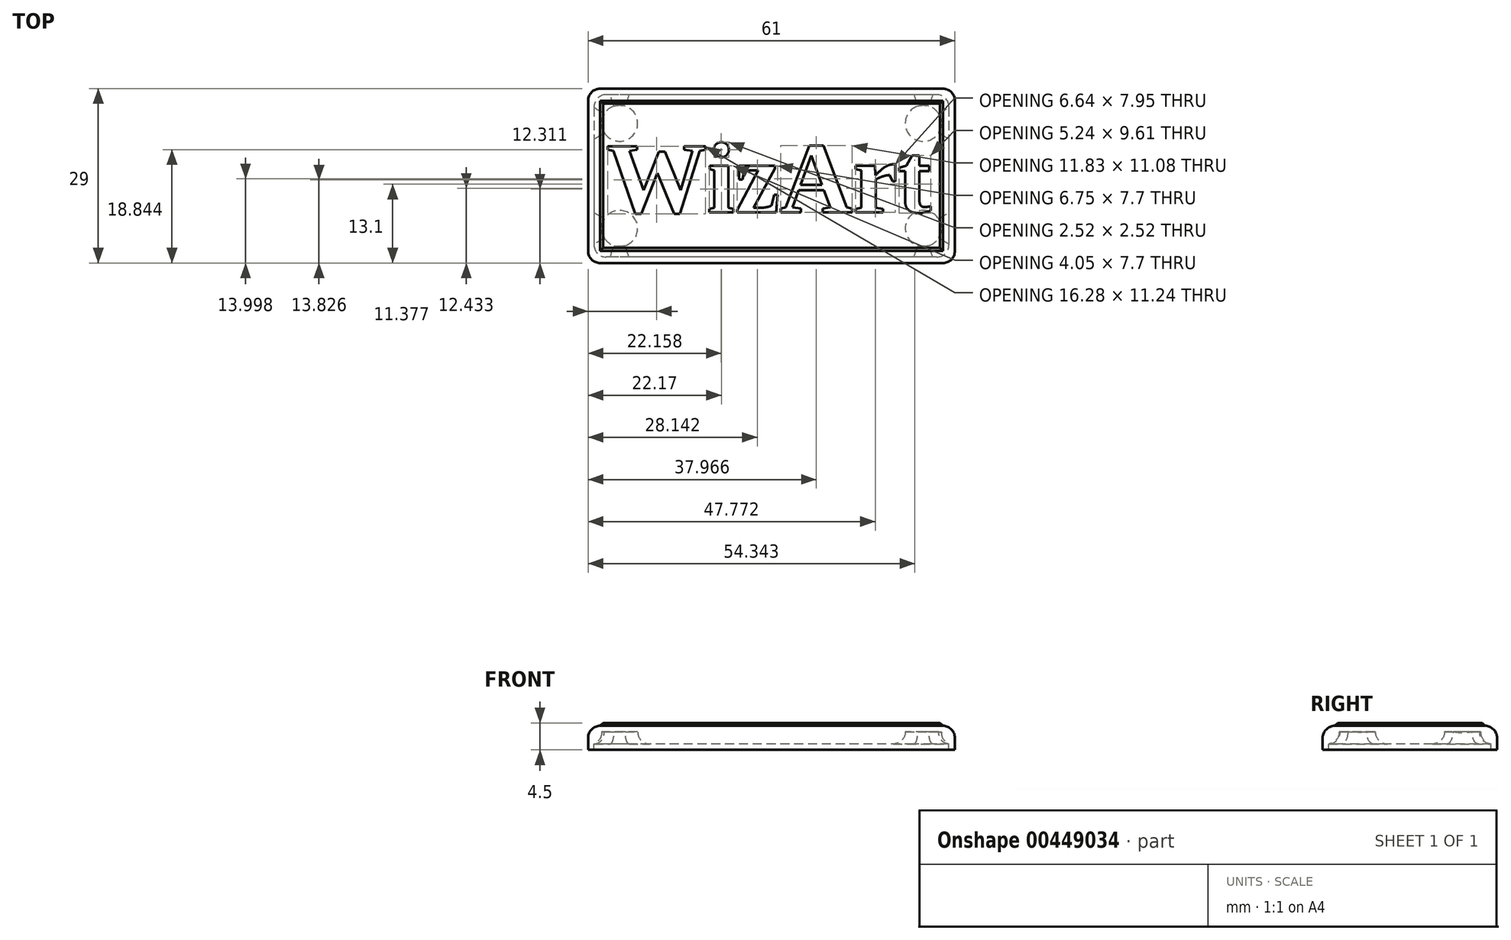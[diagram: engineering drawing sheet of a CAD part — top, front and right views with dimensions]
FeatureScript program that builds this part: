
annotation { "Feature Type Name" : "Feature", "Feature Type Description" : "" }
export const myFeature = defineFeature(function(context is Context, id is Id, definition is map)
    precondition{}
    {
        {
            var Q0;
            Q0=qCreatedBy(makeId("Top.planeOp"),FACE);
            var sketch = newSketch(context, id + "F0", { "sketchPlane" : qUnion([Q0])});
            skLineSegment(sketch, "E0.bottom", {"start": v(30.5, 14.5) * mm, "end": v(-30.5, 14.5) * mm});
            skLineSegment(sketch, "E0.top", {"start": v(30.5, -14.5) * mm, "end": v(-30.5, -14.5) * mm});
            skLineSegment(sketch, "E0.left", {"start": v(30.5, 14.5) * mm, "end": v(30.5, -14.5) * mm});
            skLineSegment(sketch, "E0.right", {"start": v(-30.5, 14.5) * mm, "end": v(-30.5, -14.5) * mm});
            skPoint(sketch, "E0.middle", {"position": v(0, 0) * mm});
            skLineSegment(sketch, "E1.bottom", {"start": v(29.5, 13.5) * mm, "end": v(-29.5, 13.5) * mm});
            skLineSegment(sketch, "E1.top", {"start": v(29.5, -13.5) * mm, "end": v(-29.5, -13.5) * mm});
            skLineSegment(sketch, "E1.left", {"start": v(29.5, 13.5) * mm, "end": v(29.5, -13.5) * mm});
            skLineSegment(sketch, "E1.right", {"start": v(-29.5, 13.5) * mm, "end": v(-29.5, -13.5) * mm});
            skLineSegment(sketch, "E2.bottom", {"start": v(25.25, 8.75) * mm, "end": v(-25.25, 8.75) * mm, "construction": true});
            skLineSegment(sketch, "E2.top", {"start": v(25.25, -8.75) * mm, "end": v(-25.25, -8.75) * mm, "construction": true});
            skLineSegment(sketch, "E2.left", {"start": v(25.25, 8.75) * mm, "end": v(25.25, -8.75) * mm, "construction": true});
            skLineSegment(sketch, "E2.right", {"start": v(-25.25, 8.75) * mm, "end": v(-25.25, -8.75) * mm, "construction": true});
            skCircle(sketch, "E3", {"center": v(-25.25, 8.75) * mm, "radius": 3 * mm});
            skCircle(sketch, "E4.MirrorC", {"center": v(25.25, 8.75) * mm, "radius": 3 * mm});
            skCircle(sketch, "E5.MirrorC", {"center": v(-25.25, -8.75) * mm, "radius": 3 * mm});
            skCircle(sketch, "E6.MirrorC", {"center": v(25.25, -8.75) * mm, "radius": 3 * mm});
            skPoint(sketch, "E7", {"position": v(-22.25, 8.75) * mm});
            skPoint(sketch, "E8", {"position": v(-22.25, -8.75) * mm});
            skPoint(sketch, "E9", {"position": v(22.25, -8.75) * mm});
            skPoint(sketch, "E10", {"position": v(22.25, 8.75) * mm});
            skSolve(sketch);
        }
        {
            var Q0;
            Q0=makeQuery(id+"F0.imprint","IMPRINT",FACE,{"disambiguationData":[TD([[makeQuery(id+"F0.imprint","IMPRINT",EDGE,{"derivedFrom":sQuery(id+"F0.wireOp",EDGE,"E1.bottom")}),1.0]])]});
            var Q1;
            Q1=makeQuery(id+"F0.imprint","IMPRINT",FACE,{"disambiguationData":[TD([[makeQuery(id+"F0.imprint","IMPRINT",EDGE,{"derivedFrom":sQuery(id+"F0.wireOp",EDGE,"E0.bottom")}),1.0]])]});
            extrude(context, id + "F1", {"entities" : qUnion([Q0, Q1]), "depth" : 2 * mm});
        }
        {
            var Q0;
            Q0=makeQuery(id+"F0.imprint","IMPRINT",FACE,{"disambiguationData":[TD([[makeQuery(id+"F0.imprint","IMPRINT",EDGE,{"derivedFrom":sQuery(id+"F0.wireOp",EDGE,"E0.bottom")}),1.0]])]});
            extrude(context, id + "F2", {"entities" : qUnion([Q0]), "operationType" : NewBodyOperationType.ADD, "oppositeDirection" : true, "depth" : 1 * mm});
        }
        {
            var Q0;
            Q0=makeQuery(id+"F1.opExtrude","CAP_FACE",FACE,{"disambiguationData":[OSD([sQuery(id+"F0.wireOp",EDGE,"E0.bottom"),sQuery(id+"F0.wireOp",EDGE,"E0.top"),sQuery(id+"F0.wireOp",EDGE,"E0.left"),sQuery(id+"F0.wireOp",EDGE,"E0.right"),sQuery(id+"F0.wireOp",EDGE,"E3"),sQuery(id+"F0.wireOp",EDGE,"E4.MirrorC"),sQuery(id+"F0.wireOp",EDGE,"E5.MirrorC"),sQuery(id+"F0.wireOp",EDGE,"E6.MirrorC")])],"isStart":false});
            var sketch = newSketch(context, id + "F3", { "sketchPlane" : qUnion([Q0])});
            skLineSegment(sketch, "E11.bottom", {"start": v(30.5, 14.5) * mm, "end": v(-30.5, 14.5) * mm});
            skLineSegment(sketch, "E11.top", {"start": v(30.5, -14.5) * mm, "end": v(-30.5, -14.5) * mm});
            skLineSegment(sketch, "E11.left", {"start": v(30.5, 14.5) * mm, "end": v(30.5, -14.5) * mm});
            skLineSegment(sketch, "E11.right", {"start": v(-30.5, 14.5) * mm, "end": v(-30.5, -14.5) * mm});
            skPoint(sketch, "E11.middle", {"position": v(0, 0) * mm});
            skSolve(sketch);
        }
        {
            var Q0;
            Q0 = qSketchRegion(id + "F3", true);
            extrude(context, id + "F4", {"entities" : qUnion([Q0]), "operationType" : NewBodyOperationType.ADD, "depth" : 1 * mm});
        }
        {
            var Q0;
            Q0=makeQuery(id+"F2.opExtrude","SWEPT_EDGE",EDGE,{"disambiguationData":[OSD([sQuery(id+"F0.wireOp",EDGE,"E1.top"),sQuery(id+"F0.wireOp",EDGE,"E1.right")])]});
            var Q1;
            Q1=makeQuery(id+"F2.opExtrude","SWEPT_EDGE",EDGE,{"disambiguationData":[OSD([sQuery(id+"F0.wireOp",EDGE,"E1.bottom"),sQuery(id+"F0.wireOp",EDGE,"E1.right")])]});
            var Q2;
            Q2=makeQuery(id+"F2.opExtrude","SWEPT_EDGE",EDGE,{"disambiguationData":[OSD([sQuery(id+"F0.wireOp",EDGE,"E1.top"),sQuery(id+"F0.wireOp",EDGE,"E1.left")])]});
            var Q3;
            Q3=makeQuery(id+"F2.opExtrude","SWEPT_EDGE",EDGE,{"disambiguationData":[OSD([sQuery(id+"F0.wireOp",EDGE,"E1.bottom"),sQuery(id+"F0.wireOp",EDGE,"E1.left")])]});
            var Q4;
            {var subQ0=sQuery(id+"F0.wireOp",EDGE,"E0.right");var subQ1=sQuery(id+"F0.wireOp",EDGE,"E0.top");Q4=makeQuery(id+"F4.boolean.opBoolean","MERGE",EDGE,{"derivedFrom":[makeQuery(id+"F2.boolean.opBoolean","MERGE",EDGE,{"derivedFrom":[makeQuery(id+"F1.opExtrude","SWEPT_EDGE",EDGE,{"disambiguationData":[OSD([subQ1,subQ0])]}),makeQuery(id+"F2.opExtrude","SWEPT_EDGE",EDGE,{"disambiguationData":[OSD([subQ1,subQ0])]})]}),makeQuery(id+"F4.opExtrude","SWEPT_EDGE",EDGE,{"disambiguationData":[OSD([sQuery(id+"F3.wireOp",EDGE,"E11.top"),sQuery(id+"F3.wireOp",EDGE,"E11.right")])]})]});}
            var Q5;
            {var subQ0=sQuery(id+"F0.wireOp",EDGE,"E0.right");var subQ1=sQuery(id+"F0.wireOp",EDGE,"E0.bottom");Q5=makeQuery(id+"F4.boolean.opBoolean","MERGE",EDGE,{"derivedFrom":[makeQuery(id+"F2.boolean.opBoolean","MERGE",EDGE,{"derivedFrom":[makeQuery(id+"F1.opExtrude","SWEPT_EDGE",EDGE,{"disambiguationData":[OSD([subQ1,subQ0])]}),makeQuery(id+"F2.opExtrude","SWEPT_EDGE",EDGE,{"disambiguationData":[OSD([subQ1,subQ0])]})]}),makeQuery(id+"F4.opExtrude","SWEPT_EDGE",EDGE,{"disambiguationData":[OSD([sQuery(id+"F3.wireOp",EDGE,"E11.bottom"),sQuery(id+"F3.wireOp",EDGE,"E11.right")])]})]});}
            var Q6;
            {var subQ0=sQuery(id+"F0.wireOp",EDGE,"E0.left");var subQ1=sQuery(id+"F0.wireOp",EDGE,"E0.bottom");Q6=makeQuery(id+"F4.boolean.opBoolean","MERGE",EDGE,{"derivedFrom":[makeQuery(id+"F2.boolean.opBoolean","MERGE",EDGE,{"derivedFrom":[makeQuery(id+"F1.opExtrude","SWEPT_EDGE",EDGE,{"disambiguationData":[OSD([subQ1,subQ0])]}),makeQuery(id+"F2.opExtrude","SWEPT_EDGE",EDGE,{"disambiguationData":[OSD([subQ1,subQ0])]})]}),makeQuery(id+"F4.opExtrude","SWEPT_EDGE",EDGE,{"disambiguationData":[OSD([sQuery(id+"F3.wireOp",EDGE,"E11.bottom"),sQuery(id+"F3.wireOp",EDGE,"E11.left")])]})]});}
            var Q7;
            {var subQ0=sQuery(id+"F0.wireOp",EDGE,"E0.left");var subQ1=sQuery(id+"F0.wireOp",EDGE,"E0.top");Q7=makeQuery(id+"F4.boolean.opBoolean","MERGE",EDGE,{"derivedFrom":[makeQuery(id+"F2.boolean.opBoolean","MERGE",EDGE,{"derivedFrom":[makeQuery(id+"F1.opExtrude","SWEPT_EDGE",EDGE,{"disambiguationData":[OSD([subQ1,subQ0])]}),makeQuery(id+"F2.opExtrude","SWEPT_EDGE",EDGE,{"disambiguationData":[OSD([subQ1,subQ0])]})]}),makeQuery(id+"F4.opExtrude","SWEPT_EDGE",EDGE,{"disambiguationData":[OSD([sQuery(id+"F3.wireOp",EDGE,"E11.top"),sQuery(id+"F3.wireOp",EDGE,"E11.left")])]})]});}
            var Q8;
            Q8=makeQuery(id+"F4.opExtrude","CAP_EDGE",EDGE,{"disambiguationData":[OSD([sQuery(id+"F3.wireOp",EDGE,"E11.bottom")])],"isStart":false});
            var Q9;
            Q9=makeQuery(id+"F4.opExtrude","CAP_FACE",FACE,{"disambiguationData":[OSD([sQuery(id+"F3.wireOp",EDGE,"E11.bottom"),sQuery(id+"F3.wireOp",EDGE,"E11.top"),sQuery(id+"F3.wireOp",EDGE,"E11.left"),sQuery(id+"F3.wireOp",EDGE,"E11.right")])],"isStart":false});
            var Q10;
            Q10=makeQuery(id+"F1.opExtrude","CAP_EDGE",EDGE,{"disambiguationData":[OSD([sQuery(id+"F0.wireOp",EDGE,"E4.MirrorC")])],"isStart":true});
            var Q11;
            Q11=makeQuery(id+"F1.opExtrude","CAP_EDGE",EDGE,{"disambiguationData":[OSD([sQuery(id+"F0.wireOp",EDGE,"E6.MirrorC")])],"isStart":true});
            var Q12;
            Q12=makeQuery(id+"F1.opExtrude","CAP_EDGE",EDGE,{"disambiguationData":[OSD([sQuery(id+"F0.wireOp",EDGE,"E3")])],"isStart":true});
            var Q13;
            Q13=makeQuery(id+"F1.opExtrude","CAP_EDGE",EDGE,{"disambiguationData":[OSD([sQuery(id+"F0.wireOp",EDGE,"E5.MirrorC")])],"isStart":true});
            fillet(context, id + "F5", {"entities" : qUnion([Q0, Q1, Q2, Q3, Q4, Q5, Q6, Q7, Q8, Q9, Q10, Q11, Q12, Q13]), "radius" : 2 * mm, "tangentPropagation" : true, "allowEdgeOverflow" : false});
        }
        {
            var Q0;
            Q0=makeQuery(id+"F4.opExtrude","CAP_FACE",FACE,{"disambiguationData":[OSD([sQuery(id+"F3.wireOp",EDGE,"E11.bottom"),sQuery(id+"F3.wireOp",EDGE,"E11.top"),sQuery(id+"F3.wireOp",EDGE,"E11.left"),sQuery(id+"F3.wireOp",EDGE,"E11.right")])],"isStart":false});
            var sketch = newSketch(context, id + "F6", { "sketchPlane" : qUnion([Q0])});
            skText(sketch, "E12", { "text": "WizArt", "fontName": "Tinos-Bold.ttf"});
            skPoint(sketch, "E13", {"position": v(28.5, 0) * mm});
            skPoint(sketch, "E14", {"position": v(0, 12.5) * mm});
            skPoint(sketch, "E15", {"position": v(0, 0) * mm});
            skLineSegment(sketch, "E16.bottom", {"start": v(-28.5, 12.5) * mm, "end": v(28.5, 12.5) * mm});
            skLineSegment(sketch, "E16.top", {"start": v(-28.5, -12.5) * mm, "end": v(28.5, -12.5) * mm});
            skLineSegment(sketch, "E16.left", {"start": v(-28.5, 12.5) * mm, "end": v(-28.5, -12.5) * mm});
            skLineSegment(sketch, "E16.right", {"start": v(28.5, 12.5) * mm, "end": v(28.5, -12.5) * mm});
            const initialGuessF6  = {"E12": [-0.0275, -0.00604, 1, 0, 0.01208]};
            skSetInitialGuess(sketch, initialGuessF6);
            skSolve(sketch);
        }
        {
            var Q0;
            Q0=makeQuery(id+"F6.imprint","IMPRINT",FACE,{"disambiguationData":[TD([[makeQuery(id+"F6.imprint","IMPRINT",EDGE,{"derivedFrom":sQuery(id+"F6.wireOp",EDGE,"E12.sketch_text.stroke-73")}),1.0]])]});
            var Q1;
            Q1=makeQuery(id+"F6.imprint","IMPRINT",FACE,{"disambiguationData":[TD([[makeQuery(id+"F6.imprint","IMPRINT",EDGE,{"derivedFrom":sQuery(id+"F6.wireOp",EDGE,"E12.sketch_text.stroke-0")}),1.0]])]});
            extrude(context, id + "F7", {"entities" : qUnion([Q0, Q1]), "depth" : 0.5 * mm});
        }
        {
            var Q0;
            Q0=makeQuery(id+"F7.opExtrude","CAP_EDGE",EDGE,{"disambiguationData":[OSD([sQuery(id+"F6.wireOp",EDGE,"E16.left")])],"isStart":false});
            var Q1;
            Q1=makeQuery(id+"F7.opExtrude","CAP_EDGE",EDGE,{"disambiguationData":[OSD([sQuery(id+"F6.wireOp",EDGE,"E16.top")])],"isStart":false});
            var Q2;
            Q2=makeQuery(id+"F7.opExtrude","CAP_EDGE",EDGE,{"disambiguationData":[OSD([sQuery(id+"F6.wireOp",EDGE,"E16.bottom")])],"isStart":false});
            var Q3;
            Q3=makeQuery(id+"F7.opExtrude","CAP_EDGE",EDGE,{"disambiguationData":[OSD([sQuery(id+"F6.wireOp",EDGE,"E16.right")])],"isStart":false});
            chamfer(context, id + "F8", {"entities" : qUnion([Q0, Q1, Q2, Q3]), "width" : 0.5 * mm, "tangentPropagation" : true});
        }
    });
